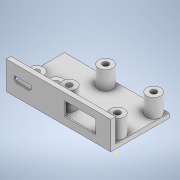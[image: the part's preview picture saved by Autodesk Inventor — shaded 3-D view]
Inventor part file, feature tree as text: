
AUTODESK INVENTOR PART (.ipt)
format: ipt  version: 2022 (Build 260153000, 153)  size: 288,768 bytes
history: native  units: mm
features: sketch x14, extrude x13
ambient origin geometry x8: Origin, YZ Plane, XZ Plane, XY Plane, X Axis, Y Axis, Z Axis, Center Point
bodies: Solid1 (feature_tree)
feature tree (27):
  extrude  "Extrusion1"  Depth=25.0mm
  extrude  "Extrusion2"  Depth=2.0mm
  extrude  "Extrusion3"  Depth=20.5mm
  extrude  "Extrusion4"  TaperAngle=0.0deg  [1 undecoded]
  extrude  "Extrusion5"  Depth=6.0mm
  extrude  "Extrusion6"  Depth=6.0mm
  extrude  "Extrusion7"  Depth=5.0mm
  extrude  "Extrusion8"  Depth=8.0mm TaperAngle=0.0deg
  extrude  "Extrusion9"  Depth=2.5mm
  extrude  "Extrusion10"  Depth=2.5mm
  extrude  "Extrusion11"  Depth=5.8mm
  extrude  "Extrusion12"  Depth=10.0mm TaperAngle=0.0deg
  extrude  "Extrusion13"  Depth=5.8mm
  sketch  "Sketch18"  dims[d36=1.0mm d37=8.3mm d38=10.0mm d39=0.0mm d40=100.0mm d41=0.0mm d42=16.0mm d43=1.3mm d44=1.5mm d45=1.5mm d46=0.0mm d49=18.0mm d50=2.0mm d51=0.0mm d52=2.0mm d53=0.0mm d54=14.0mm d55=10.0mm d56=10.0mm d57=8.3mm d58=6.0mm d59=6.0mm d60=2.85mm d61=1.9mm d62=0.0mm d63=2.5mm d64=2.5mm d65=4.0mm d66=0.0mm d68=7.4mm d69=2.3mm d70=2.65mm d71=1.4mm d75=1.0mm d76=1.0mm d77=135.0deg d78=4.0mm d79=0.0mm d80=1.6mm d81=8.0mm d82=1.0mm d83=1.0mm d84=1.0mm d85=1.5mm d86=0.0mm]
  sketch  "Sketch1"  dims[d0=30.0mm d1=25.0mm]
  sketch  "Sketch2"  dims[d2=2.0mm d3=0.0mm d4=15.5mm]
  sketch  "Sketch3"  dims[d5=15.5mm d6=20.5mm]
  sketch  "Sketch4"  dims[d7=20.5mm d8=0.0mm]
  sketch  "Sketch5"  dims[d9=0.0mm d10=6.0mm]
  sketch  "Sketch6"  dims[d11=6.0mm d12=6.0mm]
  sketch  "Sketch7"  dims[d13=6.0mm d14=5.0mm]
  sketch  "Sketch12"  dims[d15=3.5mm d16=8.0mm d17=0.0mm]
  sketch  "Sketch13"  dims[d18=2.5mm d19=2.5mm]
  sketch  "Sketch14"  dims[d20=2.5mm d21=2.5mm]
  sketch  "Sketch15"  dims[d22=4.0mm d23=0.0mm d28=5.8mm]
  sketch  "Sketch16"  dims[d29=2.0mm d30=10.0mm d31=0.0mm]
  sketch  "Sketch17"  dims[d32=13.4mm d33=5.8mm]
note: 1 required parameter value undecoded (feature->parameter linkage not recoverable at this tier; creation-order binding heuristic only, values carry confidence <= 0.55)
